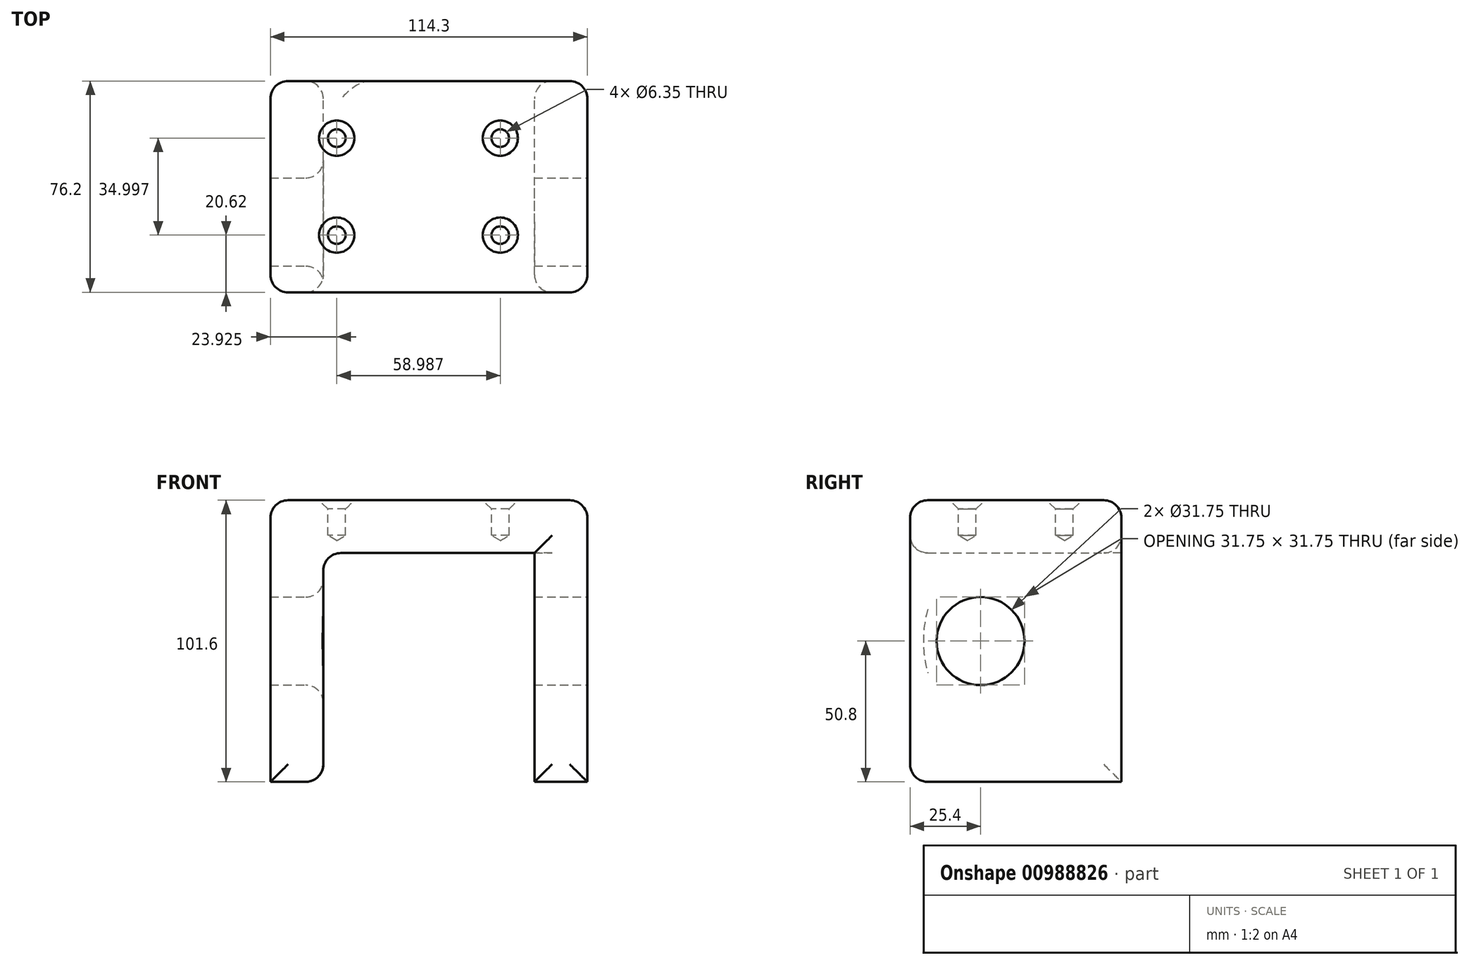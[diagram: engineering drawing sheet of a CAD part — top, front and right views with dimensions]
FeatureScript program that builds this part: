
annotation { "Feature Type Name" : "Feature", "Feature Type Description" : "" }
export const myFeature = defineFeature(function(context is Context, id is Id, definition is map)
    precondition{}
    {
        {
            var Q0;
            Q0=qCreatedBy(makeId("Front.planeOp"),FACE);
            var sketch = newSketch(context, id + "F0", { "sketchPlane" : qUnion([Q0])});
            skLineSegment(sketch, "E0", {"start": v(-57.15, 50.8) * mm, "end": v(57.15, 50.8) * mm});
            skLineSegment(sketch, "E1", {"start": v(57.15, 50.8) * mm, "end": v(57.15, -50.8) * mm});
            skLineSegment(sketch, "E2", {"start": v(57.15, -50.8) * mm, "end": v(38.1, -50.8) * mm});
            skLineSegment(sketch, "E3", {"start": v(38.1, -50.8) * mm, "end": v(38.1, 31.75) * mm});
            skLineSegment(sketch, "E4", {"start": v(38.1, 31.75) * mm, "end": v(-38.1, 31.75) * mm});
            skLineSegment(sketch, "E5", {"start": v(-38.1, 31.75) * mm, "end": v(-38.1, -50.8) * mm});
            skLineSegment(sketch, "E6", {"start": v(-38.1, -50.8) * mm, "end": v(-57.15, -50.8) * mm});
            skLineSegment(sketch, "E7", {"start": v(-57.15, -50.8) * mm, "end": v(-57.15, 50.8) * mm});
            skSolve(sketch);
        }
        {
            var Q0;
            Q0=makeQuery(id+"F0.imprint","IMPRINT",FACE,{"disambiguationData":[TD([[makeQuery(id+"F0.imprint","IMPRINT",EDGE,{"derivedFrom":sQuery(id+"F0.wireOp",EDGE,"E0")}),-1.0]])]});
            extrude(context, id + "F1", {"entities" : qUnion([Q0]), "endBound" : BoundingType.SYMMETRIC, "depth" : 76.2 * mm, "offsetDistance" : 25.4 * mm});
        }
        {
            var Q0;
            Q0=makeQuery(id+"F1.opExtrude","SWEPT_FACE",FACE,{"disambiguationData":[OSD([sQuery(id+"F0.wireOp",EDGE,"E1")])]});
            var sketch = newSketch(context, id + "F2", { "sketchPlane" : qUnion([Q0])});
            skCircle(sketch, "E8", {"center": v(-12.7, 0) * mm, "radius": 12.7 * mm});
            skSolve(sketch);
        }
        {
            var Q0;
            Q0=sQuery(id+"F2.wireOp",VERTEX,"E8.center");
            var Q1;
            Q1=makeQuery(id+"F1.opExtrude","SWEPT_BODY",BODY,{"disambiguationData":[OSD([sQuery(id+"F0.wireOp",EDGE,"E0"),sQuery(id+"F0.wireOp",EDGE,"E1"),sQuery(id+"F0.wireOp",EDGE,"E2"),sQuery(id+"F0.wireOp",EDGE,"E3"),sQuery(id+"F0.wireOp",EDGE,"E4"),sQuery(id+"F0.wireOp",EDGE,"E5"),sQuery(id+"F0.wireOp",EDGE,"E6"),sQuery(id+"F0.wireOp",EDGE,"E7")])]});
            hole(context, id + "F3", {"style" : HoleStyle.SIMPLE, "endStyle" : HoleEndStyle.THROUGH, "holeDiameter" : 31.75 * mm, "majorDiameter" : 6.35 * mm, "isTappedThrough" : true, "tappedDepth" : 12.7 * mm, "tapClearance" : 3, "startFromSketch" : true, "locations" : qUnion([Q0]), "scope" : qUnion([Q1])});
        }
        {
            var Q0;
            Q0=makeQuery(id+"F1.opExtrude","CAP_FACE",FACE,{"disambiguationData":[OSD([sQuery(id+"F0.wireOp",EDGE,"E0"),sQuery(id+"F0.wireOp",EDGE,"E1"),sQuery(id+"F0.wireOp",EDGE,"E2"),sQuery(id+"F0.wireOp",EDGE,"E3"),sQuery(id+"F0.wireOp",EDGE,"E4"),sQuery(id+"F0.wireOp",EDGE,"E5"),sQuery(id+"F0.wireOp",EDGE,"E6"),sQuery(id+"F0.wireOp",EDGE,"E7")])],"isStart":false});
            var Q1;
            Q1=makeQuery(id+"F1.opExtrude","SWEPT_EDGE",EDGE,{"disambiguationData":[OSD([sQuery(id+"F0.wireOp",EDGE,"E0"),sQuery(id+"F0.wireOp",EDGE,"E7")])]});
            var Q2;
            Q2=makeQuery(id+"F1.opExtrude","CAP_EDGE",EDGE,{"disambiguationData":[OSD([sQuery(id+"F0.wireOp",EDGE,"E0")])],"isStart":true});
            var Q3;
            Q3=makeQuery(id+"F1.opExtrude","SWEPT_EDGE",EDGE,{"disambiguationData":[OSD([sQuery(id+"F0.wireOp",EDGE,"E0"),sQuery(id+"F0.wireOp",EDGE,"E1")])]});
            var Q4;
            Q4=makeQuery(id+"F1.opExtrude","CAP_EDGE",EDGE,{"disambiguationData":[OSD([sQuery(id+"F0.wireOp",EDGE,"E1")])],"isStart":true});
            var Q5;
            Q5=makeQuery(id+"F1.opExtrude","SWEPT_FACE",FACE,{"disambiguationData":[OSD([sQuery(id+"F0.wireOp",EDGE,"E5")])]});
            var Q6;
            Q6=makeQuery(id+"F1.opExtrude","CAP_EDGE",EDGE,{"disambiguationData":[OSD([sQuery(id+"F0.wireOp",EDGE,"E7")])],"isStart":true});
            var Q7;
            Q7=makeQuery(id+"F1.opExtrude","CAP_EDGE",EDGE,{"disambiguationData":[OSD([sQuery(id+"F0.wireOp",EDGE,"E3")])],"isStart":true});
            fillet(context, id + "F4", {"entities" : qUnion([Q0, Q1, Q2, Q3, Q4, Q5, Q6, Q7]), "radius" : 6.35 * mm, "tangentPropagation" : true, "allowEdgeOverflow" : false});
        }
        {
            var Q0;
            Q0=makeQuery(id+"F1.opExtrude","SWEPT_FACE",FACE,{"disambiguationData":[OSD([sQuery(id+"F0.wireOp",EDGE,"E0")])]});
            var sketch = newSketch(context, id + "F5", { "sketchPlane" : qUnion([Q0])});
            skLineSegment(sketch, "E9.bottom", {"start": v(-33.22, 17.52) * mm, "end": v(25.76, 17.52) * mm});
            skLineSegment(sketch, "E9.top", {"start": v(-33.22, -17.48) * mm, "end": v(25.76, -17.48) * mm});
            skLineSegment(sketch, "E9.left", {"start": v(-33.22, 17.52) * mm, "end": v(-33.22, -17.48) * mm});
            skLineSegment(sketch, "E9.right", {"start": v(25.76, 17.52) * mm, "end": v(25.76, -17.48) * mm});
            skSolve(sketch);
        }
        {
            var Q0;
            Q0=sQuery(id+"F5.wireOp",VERTEX,"E9.bottom.start");
            var Q1;
            Q1=sQuery(id+"F5.wireOp",VERTEX,"E9.bottom.end");
            var Q2;
            Q2=sQuery(id+"F5.wireOp",VERTEX,"E9.top.end");
            var Q3;
            Q3=sQuery(id+"F5.wireOp",VERTEX,"E9.top.start");
            var Q4;
            Q4=makeQuery(id+"F1.opExtrude","SWEPT_BODY",BODY,{"disambiguationData":[OSD([sQuery(id+"F0.wireOp",EDGE,"E0"),sQuery(id+"F0.wireOp",EDGE,"E1"),sQuery(id+"F0.wireOp",EDGE,"E2"),sQuery(id+"F0.wireOp",EDGE,"E3"),sQuery(id+"F0.wireOp",EDGE,"E4"),sQuery(id+"F0.wireOp",EDGE,"E5"),sQuery(id+"F0.wireOp",EDGE,"E6"),sQuery(id+"F0.wireOp",EDGE,"E7")])]});
            hole(context, id + "F6", {"style" : HoleStyle.C_SINK, "endStyle" : HoleEndStyle.BLIND, "holeDiameter" : 6.35 * mm, "cSinkDiameter" : 12.7 * mm, "cSinkAngle" : 90 * degree, "majorDiameter" : 6.35 * mm, "holeDepth" : 12.7 * mm, "isTappedThrough" : true, "tappedDepth" : 12.7 * mm, "tapClearance" : 3, "startFromSketch" : true, "locations" : qUnion([Q0, Q1, Q2, Q3]), "scope" : qUnion([Q4])});
        }
    });
